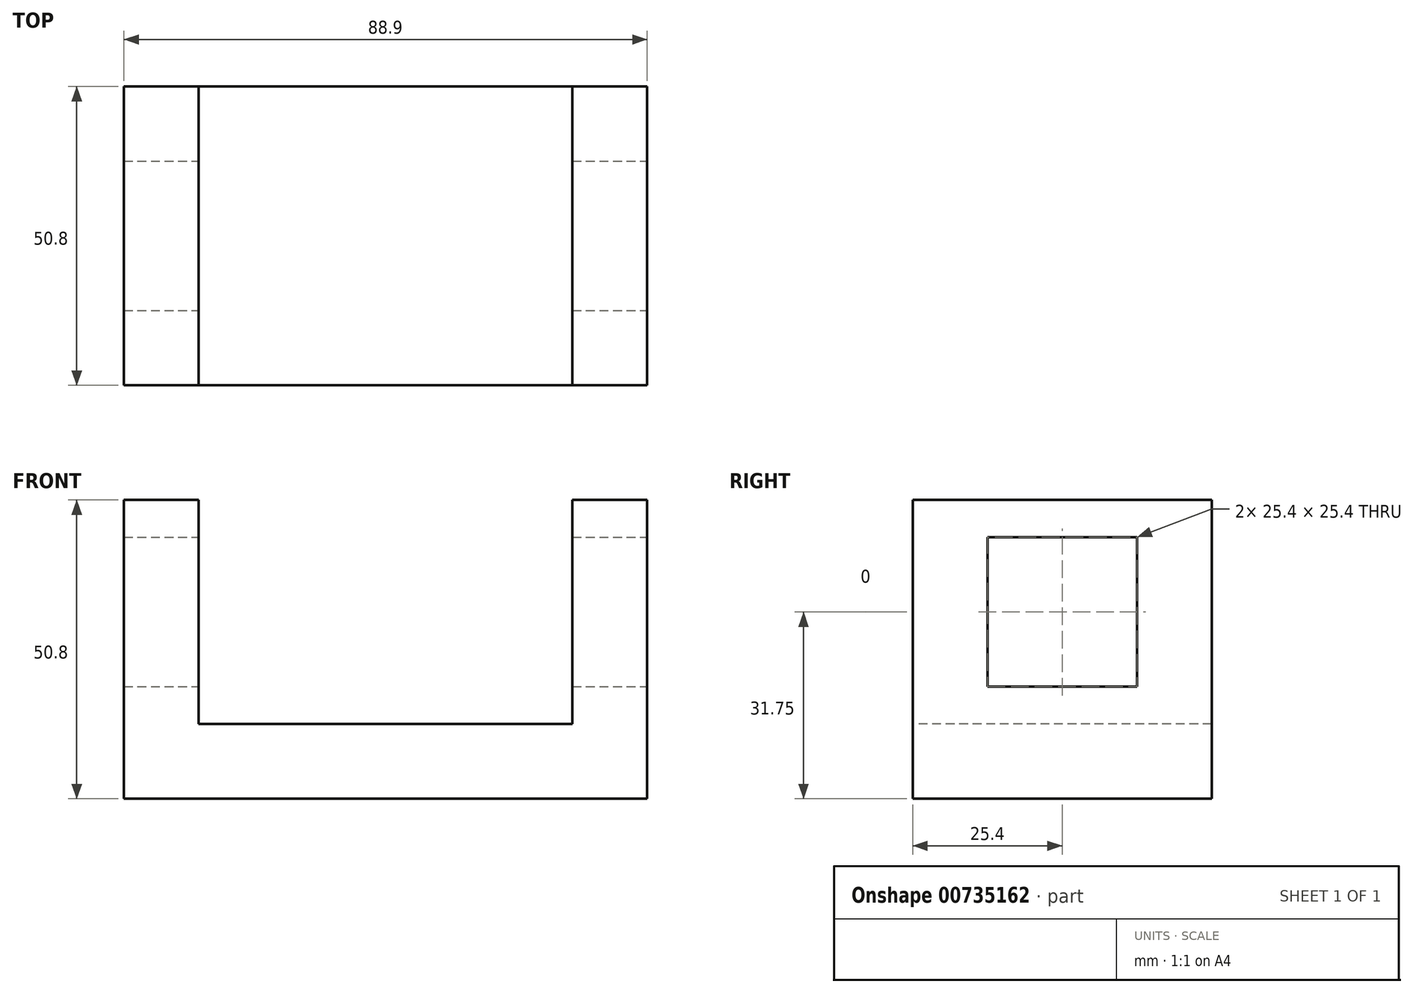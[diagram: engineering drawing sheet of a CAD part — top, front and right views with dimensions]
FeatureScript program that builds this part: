
annotation { "Feature Type Name" : "Feature", "Feature Type Description" : "" }
export const myFeature = defineFeature(function(context is Context, id is Id, definition is map)
    precondition{}
    {
        {
            var Q0;
            Q0=qCreatedBy(makeId("Right.planeOp"),FACE);
            var sketch = newSketch(context, id + "F0", { "sketchPlane" : qUnion([Q0])});
            skLineSegment(sketch, "E0.bottom", {"start": v(25.4, 25.4) * mm, "end": v(-25.4, 25.4) * mm});
            skLineSegment(sketch, "E0.top", {"start": v(25.4, -25.4) * mm, "end": v(-25.4, -25.4) * mm});
            skLineSegment(sketch, "E0.left", {"start": v(25.4, 25.4) * mm, "end": v(25.4, -25.4) * mm});
            skLineSegment(sketch, "E0.right", {"start": v(-25.4, 25.4) * mm, "end": v(-25.4, -25.4) * mm});
            skLineSegment(sketch, "E1.bottom", {"start": v(-12.7, 19.05) * mm, "end": v(12.7, 19.05) * mm});
            skLineSegment(sketch, "E1.top", {"start": v(-12.7, -6.35) * mm, "end": v(12.7, -6.35) * mm});
            skLineSegment(sketch, "E1.left", {"start": v(-12.7, 19.05) * mm, "end": v(-12.7, -6.35) * mm});
            skLineSegment(sketch, "E1.right", {"start": v(12.7, 19.05) * mm, "end": v(12.7, -6.35) * mm});
            skSolve(sketch);
        }
        {
            var Q0;
            Q0=makeQuery(id+"F0.imprint","IMPRINT",FACE,{"disambiguationData":[TD([[makeQuery(id+"F0.imprint","IMPRINT",EDGE,{"derivedFrom":sQuery(id+"F0.wireOp",EDGE,"E0.bottom")}),1.0]])]});
            extrude(context, id + "F1", {"entities" : qUnion([Q0]), "oppositeDirection" : true, "depth" : 88.9 * mm, "offsetDistance" : 25.4 * mm});
        }
        {
            var Q0;
            Q0=makeQuery(id+"F1.opExtrude","SWEPT_FACE",FACE,{"disambiguationData":[OSD([sQuery(id+"F0.wireOp",EDGE,"E0.right")])]});
            var sketch = newSketch(context, id + "F2", { "sketchPlane" : qUnion([Q0])});
            skLineSegment(sketch, "E2", {"start": v(-88.9, -25.4) * mm, "end": v(0, -25.4) * mm});
            skLineSegment(sketch, "E3", {"start": v(0, 25.4) * mm, "end": v(0, -25.4) * mm});
            skLineSegment(sketch, "E4", {"start": v(-88.9, 25.4) * mm, "end": v(-88.9, -25.4) * mm});
            skLineSegment(sketch, "E5", {"start": v(-88.9, 25.4) * mm, "end": v(-76.2, 25.4) * mm});
            skLineSegment(sketch, "E6", {"start": v(0, 25.4) * mm, "end": v(-12.7, 25.4) * mm});
            skLineSegment(sketch, "E7", {"start": v(-76.2, 25.4) * mm, "end": v(-76.2, -12.7) * mm});
            skLineSegment(sketch, "E8", {"start": v(-12.7, 25.4) * mm, "end": v(-12.7, -12.7) * mm});
            skLineSegment(sketch, "E9", {"start": v(-12.7, -12.7) * mm, "end": v(-76.2, -12.7) * mm});
            skSolve(sketch);
        }
        {
            var Q0;
            {var subQ0=sQuery(id+"F2.wireOp",EDGE,"E7");Q0=makeQuery(id+"F2.imprint","IMPRINT",FACE,{"disambiguationData":[TD([[makeQuery(id+"F2.imprint","IMPRINT",EDGE,{"derivedFrom":subQ0}),1.0]])]});}
            extrude(context, id + "F3", {"entities" : qUnion([Q0]), "operationType" : NewBodyOperationType.REMOVE, "endBound" : BoundingType.THROUGH_ALL, "oppositeDirection" : true, "depth" : 46.74 * mm, "offsetDistance" : 25.4 * mm});
        }
    });
